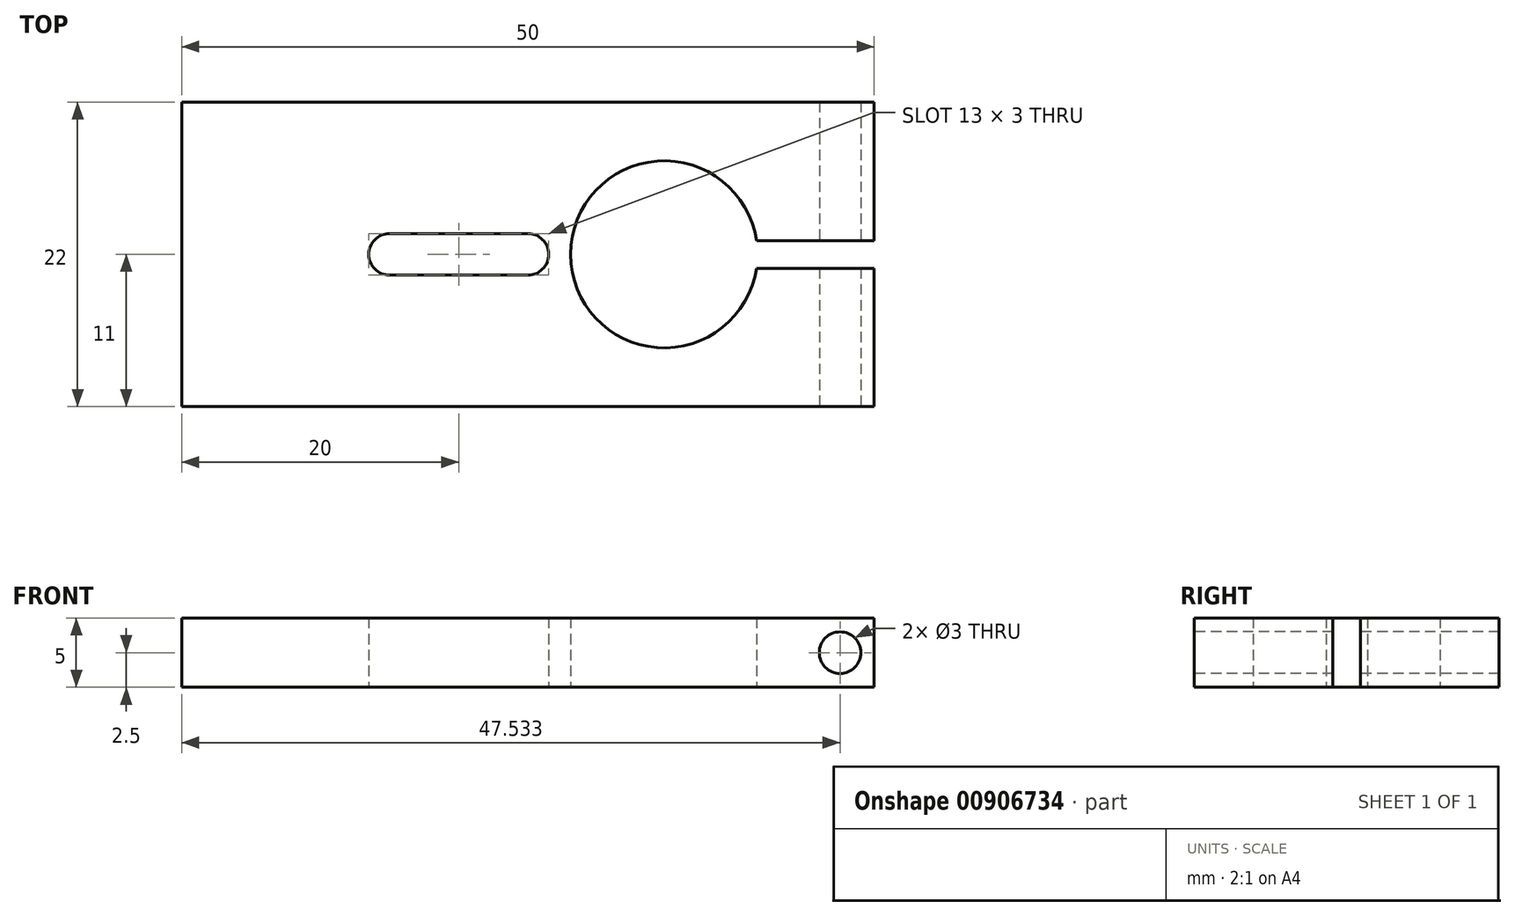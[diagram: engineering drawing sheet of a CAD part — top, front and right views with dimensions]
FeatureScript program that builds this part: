
annotation { "Feature Type Name" : "Feature", "Feature Type Description" : "" }
export const myFeature = defineFeature(function(context is Context, id is Id, definition is map)
    precondition{}
    {
        {
            var Q0;
            Q0=qCreatedBy(makeId("Top.planeOp"),FACE);
            var sketch = newSketch(context, id + "F0", { "sketchPlane" : qUnion([Q0])});
            skLineSegment(sketch, "E0.bottom", {"start": v(-25, 11) * mm, "end": v(25, 11) * mm});
            skLineSegment(sketch, "E0.top", {"start": v(-25, -11) * mm, "end": v(25, -11) * mm});
            skLineSegment(sketch, "E0.left", {"start": v(-25, 11) * mm, "end": v(-25, -11) * mm});
            skPoint(sketch, "E0.middle", {"position": v(0, 0) * mm});
            skLineSegment(sketch, "E1", {"start": v(25, 11) * mm, "end": v(25, 1) * mm});
            skArc(sketch, "E2", {"start": v(16.5, 1) * mm, "mid": v(3.07, 0) * mm, "end": v(16.5, -1) * mm});
            skLineSegment(sketch, "E3", {"start": v(25, -11) * mm, "end": v(25, -1) * mm});
            skLineSegment(sketch, "E4", {"start": v(25, -1) * mm, "end": v(16.5, -1) * mm});
            skLineSegment(sketch, "E5", {"start": v(25, 1) * mm, "end": v(16.5, 1) * mm});
            skLineSegment(sketch, "E6", {"start": v(-10, 1.5) * mm, "end": v(0, 1.5) * mm});
            skLineSegment(sketch, "E7", {"start": v(-10, -1.5) * mm, "end": v(0, -1.5) * mm});
            skArc(sketch, "E8", {"start": v(0, -1.5) * mm, "mid": v(1.5, 0) * mm, "end": v(0, 1.5) * mm});
            skArc(sketch, "E9", {"start": v(-10, 1.5) * mm, "mid": v(-11.5, 0) * mm, "end": v(-10, -1.5) * mm});
            skSolve(sketch);
        }
        {
            var Q0;
            Q0=makeQuery(id+"F0.imprint","IMPRINT",FACE,{"disambiguationData":[TD([[makeQuery(id+"F0.imprint","IMPRINT",EDGE,{"derivedFrom":sQuery(id+"F0.wireOp",EDGE,"E0.bottom")}),-1.0]])]});
            extrude(context, id + "F1", {"entities" : qUnion([Q0]), "depth" : 5 * mm, "offsetDistance" : 25 * mm});
        }
        {
            var Q0;
            Q0=makeQuery(id+"F1.opExtrude","SWEPT_FACE",FACE,{"disambiguationData":[OSD([sQuery(id+"F0.wireOp",EDGE,"E0.top")])]});
            var sketch = newSketch(context, id + "F2", { "sketchPlane" : qUnion([Q0])});
            skCircle(sketch, "E10", {"center": v(22.53, 2.5) * mm, "radius": 1.5 * mm});
            skPoint(sketch, "E10.centerSnap0", {"position": v(25, 2.5) * mm});
            skSolve(sketch);
        }
        {
            var Q0;
            Q0=sQuery(id+"F2.wireOp",VERTEX,"E10.center");
            var Q1;
            Q1=makeQuery(id+"F1.opExtrude","SWEPT_BODY",BODY,{"disambiguationData":[OSD([sQuery(id+"F0.wireOp",EDGE,"E0.bottom"),sQuery(id+"F0.wireOp",EDGE,"E0.top"),sQuery(id+"F0.wireOp",EDGE,"E0.left"),sQuery(id+"F0.wireOp",EDGE,"E1"),sQuery(id+"F0.wireOp",EDGE,"E2"),sQuery(id+"F0.wireOp",EDGE,"E3"),sQuery(id+"F0.wireOp",EDGE,"E4"),sQuery(id+"F0.wireOp",EDGE,"E5"),sQuery(id+"F0.wireOp",EDGE,"E6"),sQuery(id+"F0.wireOp",EDGE,"E7"),sQuery(id+"F0.wireOp",EDGE,"E8"),sQuery(id+"F0.wireOp",EDGE,"E9")])]});
            hole(context, id + "F3", {"style" : HoleStyle.SIMPLE, "endStyle" : HoleEndStyle.THROUGH, "holeDiameter" : 3 * mm, "majorDiameter" : 5 * mm, "isTappedThrough" : true, "tappedDepth" : 12 * mm, "tapClearance" : 3, "locations" : qUnion([Q0]), "scope" : qUnion([Q1])});
        }
    });
